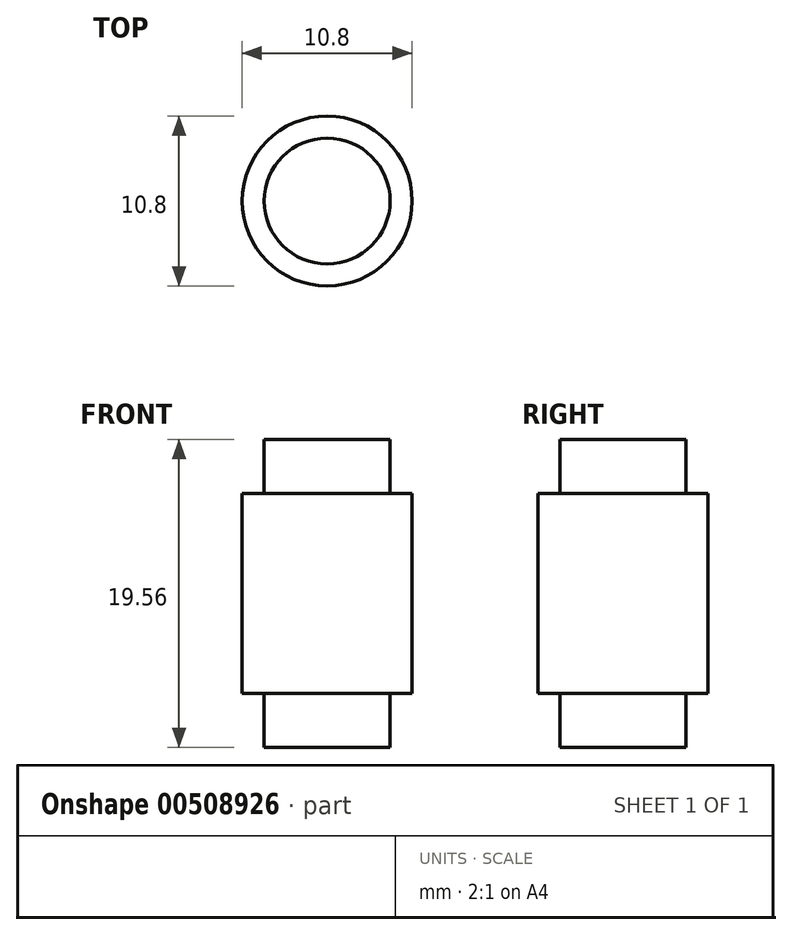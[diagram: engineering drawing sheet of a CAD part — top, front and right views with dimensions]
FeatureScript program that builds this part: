
annotation { "Feature Type Name" : "Feature", "Feature Type Description" : "" }
export const myFeature = defineFeature(function(context is Context, id is Id, definition is map)
    precondition{}
    {
        {
            var Q0;
            Q0=qCreatedBy(makeId("Top.planeOp"),FACE);
            var sketch = newSketch(context, id + "F0", { "sketchPlane" : qUnion([Q0])});
            skCircle(sketch, "E0", {"center": v(0, 0) * mm, "radius": 5.4 * mm});
            skSolve(sketch);
        }
        {
            var Q0;
            Q0 = qSketchRegion(id + "F0", true);
            extrude(context, id + "F1", {"entities" : qUnion([Q0]), "endBound" : BoundingType.SYMMETRIC, "depth" : 12.7 * mm});
        }
        {
            var Q0;
            Q0=makeQuery(id+"F1.opExtrude","CAP_FACE",FACE,{"disambiguationData":[OSD([sQuery(id+"F0.wireOp",EDGE,"E0")])],"isStart":false});
            var sketch = newSketch(context, id + "F2", { "sketchPlane" : qUnion([Q0])});
            skCircle(sketch, "E1", {"center": v(0, 0) * mm, "radius": 4 * mm});
            skSolve(sketch);
        }
        {
            var Q0;
            Q0 = qSketchRegion(id + "F2", true);
            extrude(context, id + "F3", {"entities" : qUnion([Q0]), "operationType" : NewBodyOperationType.ADD, "depth" : 3.43 * mm});
        }
        {
            var Q0;
            Q0=makeQuery(id+"F1.opExtrude","CAP_FACE",FACE,{"disambiguationData":[OSD([sQuery(id+"F0.wireOp",EDGE,"E0")])],"isStart":true});
            var sketch = newSketch(context, id + "F4", { "sketchPlane" : qUnion([Q0])});
            skCircle(sketch, "E2", {"center": v(0, 0) * mm, "radius": 4 * mm});
            skSolve(sketch);
        }
        {
            var Q0;
            Q0 = qSketchRegion(id + "F4", true);
            extrude(context, id + "F5", {"entities" : qUnion([Q0]), "operationType" : NewBodyOperationType.ADD, "depth" : 3.43 * mm});
        }
    });
